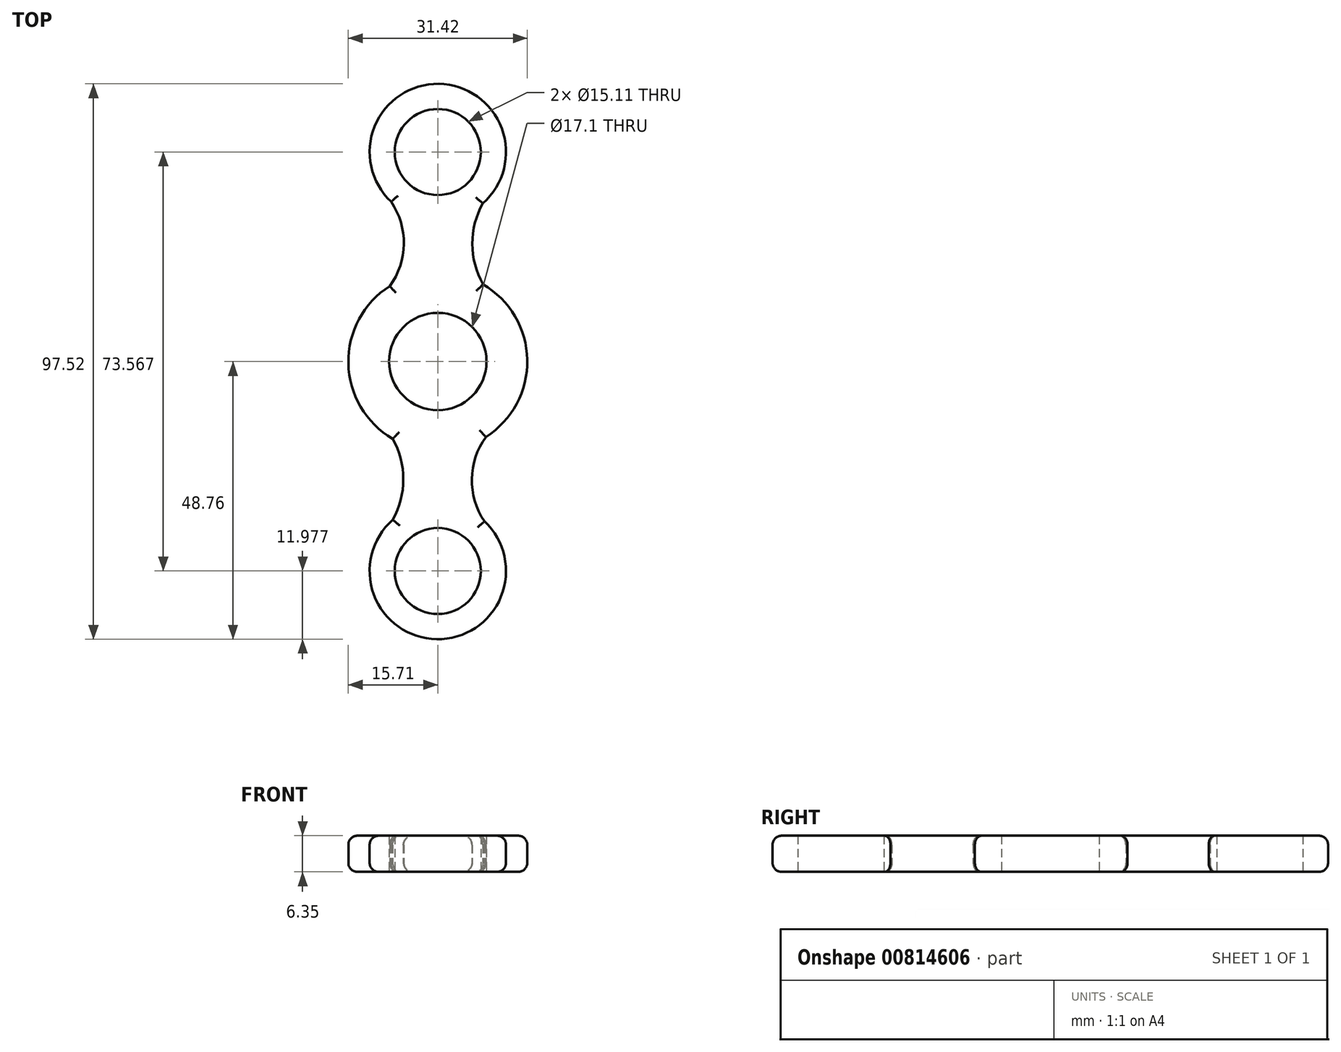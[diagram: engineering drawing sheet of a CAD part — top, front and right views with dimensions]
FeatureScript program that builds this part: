
annotation { "Feature Type Name" : "Feature", "Feature Type Description" : "" }
export const myFeature = defineFeature(function(context is Context, id is Id, definition is map)
    precondition{}
    {
        {
            var Q0;
            Q0=qCreatedBy(makeId("Top.planeOp"),FACE);
            var sketch = newSketch(context, id + "F0", { "sketchPlane" : qUnion([Q0])});
            skCircle(sketch, "E0", {"center": v(0, 0) * mm, "radius": 8.55 * mm});
            skCircle(sketch, "E1", {"center": v(0, 36.78) * mm, "radius": 7.56 * mm});
            skArc(sketch, "E2", {"start": v(7.9, 27.8) * mm, "mid": v(0.2, 48.75) * mm, "end": v(-8.2, 28.06) * mm});
            skArc(sketch, "E3", {"start": v(-8.44, 13.25) * mm, "mid": v(-15.7, -0.3) * mm, "end": v(-7.93, -13.56) * mm});
            skArc(sketch, "E4", {"start": v(7.9, 27.8) * mm, "mid": v(6.06, 20.67) * mm, "end": v(7.93, 13.56) * mm});
            skArc(sketch, "E5", {"start": v(-8.44, 13.25) * mm, "mid": v(-5.96, 20.62) * mm, "end": v(-8.2, 28.06) * mm});
            skArc(sketch, "E6.1.0", {"start": v(-7.9, -27.8) * mm, "mid": v(-0.2, -48.75) * mm, "end": v(8.2, -28.06) * mm});
            skArc(sketch, "E6.1.1", {"start": v(-7.9, -27.8) * mm, "mid": v(-6.06, -20.67) * mm, "end": v(-7.93, -13.56) * mm});
            skArc(sketch, "E6.1.2", {"start": v(8.44, -13.25) * mm, "mid": v(5.96, -20.62) * mm, "end": v(8.2, -28.06) * mm});
            skCircle(sketch, "E6.1.3", {"center": v(0, -36.78) * mm, "radius": 7.56 * mm});
            skArc(sketch, "E7.trimOffspring", {"start": v(8.44, -13.25) * mm, "mid": v(15.7, 0.3) * mm, "end": v(7.93, 13.56) * mm});
            skSolve(sketch);
        }
        {
            var Q0;
            Q0=makeQuery(id+"F0.imprint","IMPRINT",FACE,{"disambiguationData":[TD([[makeQuery(id+"F0.imprint","IMPRINT",EDGE,{"derivedFrom":sQuery(id+"F0.wireOp",EDGE,"E0")}),-1.0]])]});
            extrude(context, id + "F1", {"entities" : qUnion([Q0]), "depth" : 6.35 * mm, "offsetDistance" : 25.4 * mm});
        }
        {
            var Q0;
            Q0=makeQuery(id+"F1.opExtrude","CAP_EDGE",EDGE,{"disambiguationData":[OSD([sQuery(id+"F0.wireOp",EDGE,"E6.1.0")])],"isStart":false});
            var Q1;
            Q1=makeQuery(id+"F1.opExtrude","CAP_EDGE",EDGE,{"disambiguationData":[OSD([sQuery(id+"F0.wireOp",EDGE,"E3")])],"isStart":false});
            var Q2;
            Q2=makeQuery(id+"F1.opExtrude","CAP_EDGE",EDGE,{"disambiguationData":[OSD([sQuery(id+"F0.wireOp",EDGE,"E2")])],"isStart":false});
            var Q3;
            Q3=makeQuery(id+"F1.opExtrude","CAP_EDGE",EDGE,{"disambiguationData":[OSD([sQuery(id+"F0.wireOp",EDGE,"E4")])],"isStart":false});
            var Q4;
            Q4=makeQuery(id+"F1.opExtrude","CAP_EDGE",EDGE,{"disambiguationData":[OSD([sQuery(id+"F0.wireOp",EDGE,"E5")])],"isStart":false});
            var Q5;
            Q5=makeQuery(id+"F1.opExtrude","CAP_EDGE",EDGE,{"disambiguationData":[OSD([sQuery(id+"F0.wireOp",EDGE,"E7.trimOffspring")])],"isStart":false});
            var Q6;
            Q6=makeQuery(id+"F1.opExtrude","CAP_EDGE",EDGE,{"disambiguationData":[OSD([sQuery(id+"F0.wireOp",EDGE,"E6.1.2")])],"isStart":false});
            var Q7;
            Q7=makeQuery(id+"F1.opExtrude","CAP_EDGE",EDGE,{"disambiguationData":[OSD([sQuery(id+"F0.wireOp",EDGE,"E6.1.1")])],"isStart":false});
            var Q8;
            Q8=makeQuery(id+"F1.opExtrude","CAP_EDGE",EDGE,{"disambiguationData":[OSD([sQuery(id+"F0.wireOp",EDGE,"E6.1.2")])],"isStart":true});
            var Q9;
            Q9=makeQuery(id+"F1.opExtrude","CAP_EDGE",EDGE,{"disambiguationData":[OSD([sQuery(id+"F0.wireOp",EDGE,"E7.trimOffspring")])],"isStart":true});
            var Q10;
            Q10=makeQuery(id+"F1.opExtrude","CAP_EDGE",EDGE,{"disambiguationData":[OSD([sQuery(id+"F0.wireOp",EDGE,"E4")])],"isStart":true});
            var Q11;
            Q11=makeQuery(id+"F1.opExtrude","CAP_EDGE",EDGE,{"disambiguationData":[OSD([sQuery(id+"F0.wireOp",EDGE,"E2")])],"isStart":true});
            var Q12;
            Q12=makeQuery(id+"F1.opExtrude","CAP_EDGE",EDGE,{"disambiguationData":[OSD([sQuery(id+"F0.wireOp",EDGE,"E5")])],"isStart":true});
            var Q13;
            Q13=makeQuery(id+"F1.opExtrude","CAP_EDGE",EDGE,{"disambiguationData":[OSD([sQuery(id+"F0.wireOp",EDGE,"E3")])],"isStart":true});
            var Q14;
            Q14=makeQuery(id+"F1.opExtrude","CAP_EDGE",EDGE,{"disambiguationData":[OSD([sQuery(id+"F0.wireOp",EDGE,"E6.1.1")])],"isStart":true});
            fillet(context, id + "F2", {"entities" : qUnion([Q0, Q1, Q2, Q3, Q4, Q5, Q6, Q7, Q8, Q9, Q10, Q11, Q12, Q13, Q14]), "radius" : 1.6 * mm, "tangentPropagation" : true, "allowEdgeOverflow" : false});
        }
        {
            var Q0;
            Q0=makeQuery(id+"F1.opExtrude","CAP_EDGE",EDGE,{"disambiguationData":[OSD([sQuery(id+"F0.wireOp",EDGE,"E6.1.0")])],"isStart":true});
            fillet(context, id + "F3", {"entities" : qUnion([Q0]), "radius" : 1.6 * mm, "tangentPropagation" : true, "allowEdgeOverflow" : false});
        }
    });
